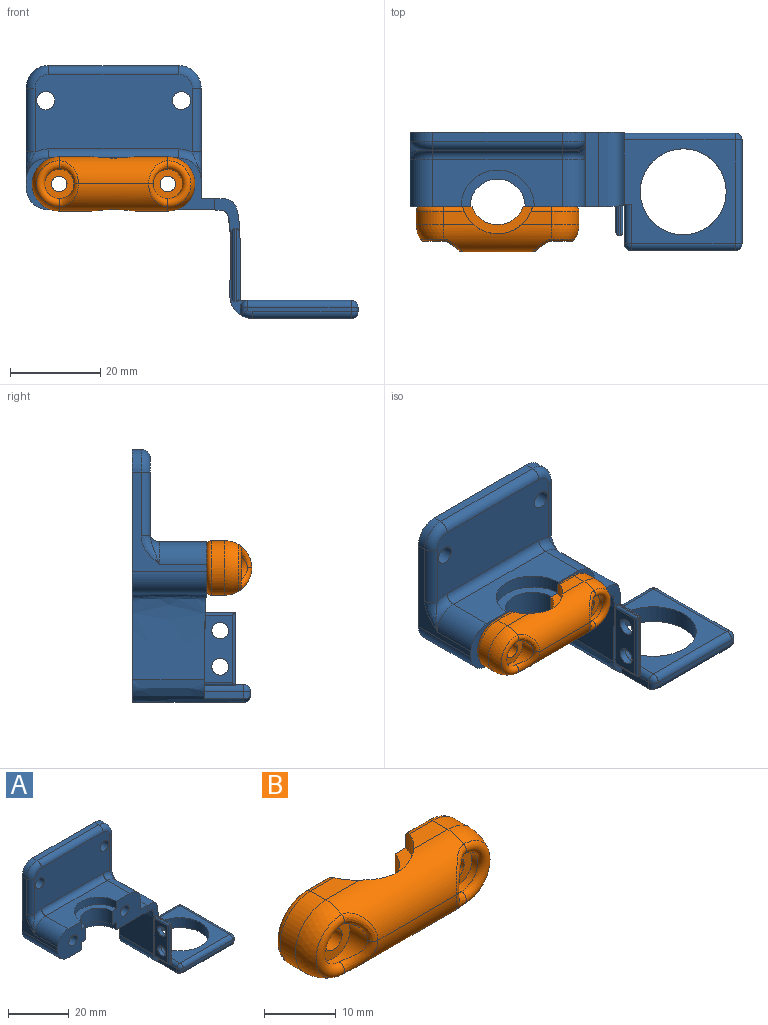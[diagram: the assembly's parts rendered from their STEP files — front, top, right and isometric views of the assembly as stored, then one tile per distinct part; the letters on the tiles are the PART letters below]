
ASSEMBLY  parts=2 mates=1
PART A: 88 faces, bbox 78x32.9x58.8 mm
  f0: bspline ~22.56x5.96mm, area 32.3mm2, adj f1,f4,f50,f52,f60,f76,f77,f78
  f1: plane 3.81x3.31mm, normal (0,-1,0), area 4.9mm2, adj f0,f55,f58,f60,f66,f75,f84,f87
  f2: plane 41.74x31.94mm, normal (0,1,0), area 1141.5mm2, adj f6,f7,f8,f13,f14,f15,f20,f21
  f3: cylinder r=6.1mm len=12.2mm, axis (0,0,-1), area 105.4mm2, adj f4,f5,f10,f16
  f4: plane 16.27x11.5mm, normal (0,-1,0), area 130.4mm2, adj f0,f3,f6,f7,f9,f10,f11,f16
  f5: plane 13.27x11.5mm, normal (0,-1,0), area 117.3mm2, adj f3,f6,f8,f9,f10,f11,f16,f17
  f6: plane 36.74x16.46mm, normal (0,0,-1), area 502mm2, adj f2,f4,f5,f11,f36,f50
  f7: plane 26.37x18.46mm, normal (1,0,0), area 114.1mm2, adj f2,f4,f35,f38,f39,f40,f49
  f8: plane 21.94x16.46mm, normal (-1,0,0), area 74.1mm2, adj f2,f5,f34,f36,f37,f47,f48
  f9: plane 28.74x10.46mm, normal (0,0,1), area 197.5mm2, adj f4,f5,f17,f37,f38,f44
  f10: plane 16.2x8.08mm, normal (0,0,-1), area 44.3mm2, adj f3,f4,f5,f11
  f11: cylinder r=8.1mm len=16.2mm, axis (0,0,-1), area 76.2mm2, adj f4,f5,f6,f10
  f12: plane 34.74x17.12mm, normal (0,-1,0), area 543.5mm2, adj f13,f14,f39,f41,f42,f43,f44,f45
  f13: cylinder r=2mm len=4mm, axis (0,-1,0), area 50.3mm2, adj f2,f12
  f14: cylinder r=2mm len=4mm, axis (0,-1,0), area 50.3mm2, adj f2,f12
  f15: plane 28.74x2mm, normal (0,0,1), area 57.5mm2, adj f2,f34,f35,f43
  f16: plane 16.2x8.1mm, normal (0,0,1), area 44.6mm2, adj f3,f4,f5,f17
  f17: cylinder r=8.1mm len=16.2mm, axis (0,0,1), area 76.3mm2, adj f4,f5,f9,f16
  f18: cylinder r=2mm len=6.46mm, axis (0,-1,0), area 81.2mm2, adj f4,f26
  f19: cylinder r=2mm len=6.46mm, axis (0,-1,0), area 81.2mm2, adj f5,f33
  f20: plane 10x3.46mm, normal (0.01,0,-1), area 34.6mm2, adj f2,f21,f25,f26
  f21: plane 10x2.98mm, normal (-0.86,0,-0.51), area 34.6mm2, adj f2,f20,f22,f26
  f22: plane 10x3.02mm, normal (-0.87,0,0.49), area 34.6mm2, adj f2,f21,f23,f26
  f23: plane 10x3.46mm, normal (-0.01,0,1), area 34.6mm2, adj f2,f22,f24,f26
  f24: plane 10x2.98mm, normal (0.86,0,0.51), area 34.6mm2, adj f2,f23,f25,f26
  f25: plane 10x3.02mm, normal (0.87,0,-0.49), area 34.6mm2, adj f2,f20,f24,f26
  f26: plane 6.93x6.05mm, normal (0,1,0), area 18.6mm2, adj f18,f20,f21,f22,f23,f24,f25
  f27: plane 10x3.46mm, normal (-0.03,0,-1), area 34.6mm2, adj f2,f28,f32,f33
  f28: plane 10x3.05mm, normal (-0.88,0,-0.47), area 34.6mm2, adj f2,f27,f29,f33
  f29: plane 10x2.95mm, normal (-0.85,0,0.53), area 34.6mm2, adj f2,f28,f30,f33
  f30: plane 10x3.46mm, normal (0.03,0,1), area 34.6mm2, adj f2,f29,f31,f33
  f31: plane 10x3.05mm, normal (0.88,0,0.47), area 34.6mm2, adj f2,f30,f32,f33
  f32: plane 10x2.95mm, normal (0.85,0,-0.53), area 34.6mm2, adj f2,f27,f31,f33
  f33: plane 6.93x6.1mm, normal (0,1,0), area 18.6mm2, adj f19,f27,f28,f29,f30,f31,f32
  f34: cylinder r=5mm len=5mm, axis (0,-1,0), area 15.7mm2, adj f2,f8,f15,f45
  f35: cylinder r=5mm len=5mm, axis (0,1,0), area 15.7mm2, adj f2,f7,f15,f41
  f36: cylinder r=5mm len=16.46mm, axis (0,-1,0), area 129.3mm2, adj f2,f5,f6,f8
  f37: cylinder r=5mm len=10.46mm, axis (0,1,0), area 82.1mm2, adj f5,f8,f9,f46
  f38: cylinder r=5mm len=10.46mm, axis (0,-1,0), area 82.1mm2, adj f4,f7,f9,f42
  f39: cylinder r=2mm len=14.12mm, axis (0,0,-1), area 44.4mm2, adj f7,f12,f40,f41
  f40: bspline ~7.51x4mm, area 7.3mm2, adj f7,f39,f42
  f41: torus R=3mm, axis (0,1,0), area 21.1mm2, adj f12,f35,f39,f43
  f42: torus R=7mm, axis (0,1,0), area 17.5mm2, adj f12,f38,f40,f44
  f43: cylinder r=2mm len=28.74mm, axis (1,0,0), area 90.3mm2, adj f12,f15,f41,f45
  f44: cylinder r=2mm len=28.74mm, axis (1,0,0), area 90.3mm2, adj f9,f12,f42,f46
  f45: torus R=3mm, axis (0,1,0), area 21.1mm2, adj f12,f34,f43,f47
  f46: torus R=7mm, axis (0,1,0), area 17.5mm2, adj f12,f37,f44,f48
  f47: cylinder r=2mm len=14.12mm, axis (0,0,1), area 44.4mm2, adj f8,f12,f45,f48
  f48: bspline ~7.51x4mm, area 7.8mm2, adj f8,f46,f47
  f49: plane 16.46x3mm, normal (0,0,1), area 49.4mm2, adj f2,f4,f7,f52
  f50: bspline ~20x16.46mm, area 341.5mm2, adj f0,f6,f51,f60
  f51: bspline ~22.56x5.96mm, area 56.1mm2, adj f2,f50,f52,f53,f60
  f52: bspline ~24.47x16.46mm, area 422.2mm2, adj f0,f49,f51,f53,f55,f61
  f53: plane 26.93x4.2mm, normal (0,1,0), area 65.2mm2, adj f51,f52,f54,f60,f61,f65
  f54: plane 24.5x21.83mm, normal (0,0,-1), area 251.3mm2, adj f53,f59,f60,f69,f73
  f55: plane 24.5x23mm, normal (0,0,1), area 267mm2, adj f1,f52,f59,f61,f62,f66,f67
  f56: plane 23x1mm, normal (0,-1,0), area 22.9mm2, adj f67,f68,f72,f73,f74
  f57: plane 23x1mm, normal (1,0,0), area 23mm2, adj f62,f65,f68,f69
  f58: plane 8.63x1.73mm, normal (-1,0,0), area 14.9mm2, adj f1,f60,f66,f72
  f59: cylinder r=9.5mm len=19mm, axis (0,0,1), area 238.8mm2, adj f54,f55
  f60: bspline ~30.86x5.01mm, area 149.1mm2, adj f0,f1,f50,f51,f53,f54,f58,f74
  f61: cylinder r=1.5mm len=24.5mm, axis (-1,0,0), area 57.7mm2, adj f52,f53,f55,f63
  f62: cylinder r=1.5mm len=23mm, axis (0,1,0), area 54.2mm2, adj f55,f57,f63,f64
  f63: sphere r=1.5mm, area 2.3mm2, adj f61,f62,f65
  f64: sphere r=1.5mm, area 3.5mm2, adj f62,f67,f68
  f65: cylinder r=1.5mm len=2.5mm, axis (0,0,-1), area 4.1mm2, adj f53,f57,f63,f69
  f66: cylinder r=1.5mm len=8.63mm, axis (0,-1,0), area 20.3mm2, adj f1,f55,f58,f70
  f67: cylinder r=1.5mm len=23mm, axis (-1,0,0), area 54.2mm2, adj f55,f56,f64,f70
  f68: cylinder r=1.5mm len=1.5mm, axis (0,0,1), area 2.4mm2, adj f56,f57,f64,f71
  f69: cylinder r=1.5mm len=24.5mm, axis (0,-1,0), area 56mm2, adj f54,f57,f65,f71
  f70: sphere r=1.5mm, area 3.5mm2, adj f66,f67,f72
  f71: sphere r=1.5mm, area 3.5mm2, adj f68,f69,f73
  f72: cylinder r=1.5mm len=1.73mm, axis (0,0,-1), area 3mm2, adj f56,f58,f70,f74
  f73: cylinder r=1.5mm len=21.83mm, axis (1,0,0), area 51.4mm2, adj f54,f56,f71,f74
  f74: torus R=3.5mm, axis (0,1,0), area 4.8mm2, adj f56,f60,f72,f73
  f75: plane 6.8x0.31mm, normal (0,0,-1), area 2.1mm2, adj f1,f79,f84,f87
  f76: plane 14.97x6.2mm, normal (-1,0,0), area 70.6mm2, adj f0,f80,f81,f82,f83,f84
  f77: plane 14.97x6.2mm, normal (1,0,0), area 70.8mm2, adj f0,f80,f81,f85,f86,f87
  f78: plane 6.67x0.32mm, normal (0,0,1), area 2.1mm2, adj f0,f79,f82,f85
  f79: plane 16.17x0.31mm, normal (0,-1,0), area 5mm2, adj f75,f78,f83,f86
  f80: cylinder r=1.85mm len=3.7mm, axis (1,0,0), area 17.6mm2, adj f76,f77
  f81: cylinder r=1.85mm len=3.7mm, axis (1,0,0), area 17.6mm2, adj f76,f77
  f82: cylinder r=0.6mm len=6.65mm, axis (0,-1,0), area 6mm2, adj f0,f76,f78,f83
  f83: cylinder r=0.6mm len=16.17mm, axis (0,0,1), area 14.7mm2, adj f76,f79,f82,f84
  f84: cylinder r=0.6mm len=6.8mm, axis (0,1,0), area 6.1mm2, adj f0,f1,f75,f76,f83
  f85: cylinder r=0.6mm len=6.68mm, axis (0,1,0), area 6mm2, adj f0,f77,f78,f86
  f86: cylinder r=0.6mm len=16.17mm, axis (0,0,-1), area 14.7mm2, adj f77,f79,f85,f87
  f87: cylinder r=0.6mm len=6.8mm, axis (0,-1,0), area 6.1mm2, adj f0,f1,f75,f77,f86
PART B: 35 faces, bbox 37x10.1x13 mm
  f0: plane 6.71x3mm, normal (0,0,-1), area 16.4mm2, adj f6,f8,f12,f33
  f1: plane 6.71x3mm, normal (0,0,-1), area 16.4mm2, adj f6,f9,f13,f33
  f2: plane 6.71x3mm, normal (0,0,1), area 16.4mm2, adj f7,f11,f12,f34
  f3: plane 6.71x3mm, normal (0,0,1), area 16.4mm2, adj f7,f10,f13,f34
  f4: plane 11.34x10mm, normal (0,1,0), area 85.3mm2, adj f9,f10,f14,f29,f30,f31,f32,f33
  f5: plane 11.34x10mm, normal (0,1,0), area 85.3mm2, adj f8,f11,f17,f28,f30,f31,f32,f33
  f6: cylinder r=6mm len=24mm, axis (-1,0,0), area 172.9mm2, adj f0,f1,f7,f20,f21,f22,f27,f33
  f7: cylinder r=6mm len=24mm, axis (1,0,0), area 172.9mm2, adj f2,f3,f6,f20,f21,f24,f25,f34
  f8: cylinder r=1mm len=4.58mm, axis (1,0,0), area 6.9mm2, adj f0,f5,f28,f33
  f9: cylinder r=1mm len=4.58mm, axis (1,0,0), area 6.9mm2, adj f1,f4,f29,f33
  f10: cylinder r=1mm len=4.58mm, axis (-1,0,0), area 6.9mm2, adj f3,f4,f29,f34
  f11: cylinder r=1mm len=4.58mm, axis (-1,0,0), area 6.9mm2, adj f2,f5,f28,f34
  f12: cylinder r=6mm len=12mm, axis (0,1,0), area 56.5mm2, adj f0,f2,f20,f28
  f13: cylinder r=6mm len=12mm, axis (0,1,0), area 56.5mm2, adj f1,f3,f21,f29
  f14: cylinder r=1.7mm len=5.5mm, axis (0,-1,0), area 58.7mm2, adj f4,f15
  f15: plane 6.5x6.5mm, normal (0,-1,0), area 24.1mm2, adj f14,f16
  f16: cylinder r=3.25mm len=6.5mm, axis (0,-1,0), area 36.2mm2, adj f15,f25,f26,f27
  f17: cylinder r=1.7mm len=5.5mm, axis (0,-1,0), area 58.7mm2, adj f5,f18
  f18: plane 6.5x6.5mm, normal (0,-1,0), area 24.1mm2, adj f17,f19
  f19: cylinder r=3.25mm len=6.5mm, axis (0,-1,0), area 36.2mm2, adj f18,f22,f23,f24
  f20: sphere r=6mm, area 59.6mm2, adj f6,f7,f12,f23
  f21: sphere r=6mm, area 59.6mm2, adj f6,f7,f13,f26
  f22: bspline ~5.34x4.83mm, area 13.1mm2, adj f6,f19,f23,f24
  f23: torus R=4.25mm, axis (0,1,0), area 32.9mm2, adj f19,f20,f22,f24
  f24: bspline ~6.05x4.83mm, area 13.1mm2, adj f7,f19,f22,f23
  f25: bspline ~6.05x4.83mm, area 13.1mm2, adj f7,f16,f26,f27
  f26: torus R=4.25mm, axis (0,1,0), area 32.9mm2, adj f16,f21,f25,f27
  f27: bspline ~6.05x4.83mm, area 13.1mm2, adj f6,f16,f25,f26
  f28: torus R=5mm, axis (0,-1,0), area 27.8mm2, adj f5,f8,f11,f12
  f29: torus R=5mm, axis (0,-1,0), area 27.8mm2, adj f4,f9,f10,f13
  f30: plane 15.49x6mm, normal (0,0,-1), area 35.9mm2, adj f4,f5,f31,f33
  f31: cylinder r=6mm len=11.31mm, axis (0,0,1), area 88.6mm2, adj f4,f5,f30,f32
  f32: plane 15.49x6mm, normal (0,0,1), area 35.9mm2, adj f4,f5,f31,f34
  f33: cylinder r=8mm len=15.49mm, axis (0,0,1), area 60.7mm2, adj f0,f1,f4,f5,f6,f8,f9,f30
  f34: cylinder r=8mm len=15.49mm, axis (0,0,1), area 60.7mm2, adj f2,f3,f4,f5,f7,f10,f11,f32
PLACE A t=(-8.78,19.77,-8.84)mm
PLACE B t=(-8.78,2.1,-3.09)mm
MATE revolute B.f13 <-> A.f18  axis (0,1,0) through (3.22,0.1,-3.09)mm
